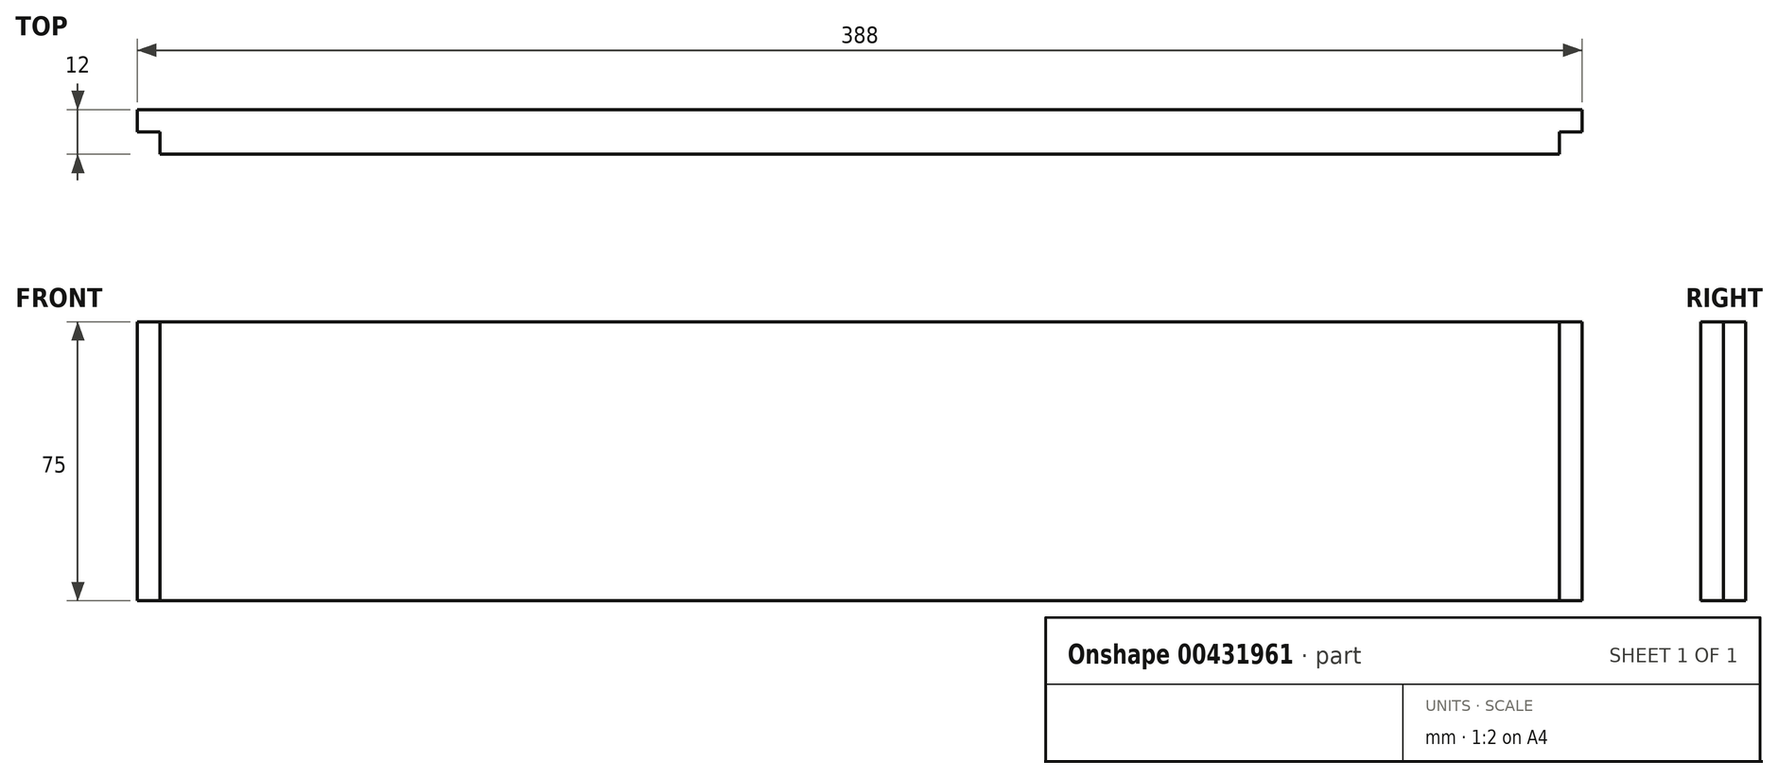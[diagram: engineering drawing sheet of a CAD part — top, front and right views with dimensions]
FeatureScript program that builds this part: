
annotation { "Feature Type Name" : "Feature", "Feature Type Description" : "" }
export const myFeature = defineFeature(function(context is Context, id is Id, definition is map)
    precondition{}
    {
        {
            var Q0;
            Q0=qCreatedBy(makeId("Front.planeOp"),FACE);
            var sketch = newSketch(context, id + "F0", { "sketchPlane" : qUnion([Q0])});
            skLineSegment(sketch, "E0.bottom", {"start": v(-183, 37.5) * mm, "end": v(205, 37.5) * mm});
            skLineSegment(sketch, "E0.top", {"start": v(-183, -37.5) * mm, "end": v(205, -37.5) * mm});
            skLineSegment(sketch, "E0.left", {"start": v(-183, 37.5) * mm, "end": v(-183, -37.5) * mm});
            skLineSegment(sketch, "E0.right", {"start": v(205, 37.5) * mm, "end": v(205, -37.5) * mm});
            skPoint(sketch, "E0.middle", {"position": v(11, 0) * mm});
            skSolve(sketch);
        }
        {
            var Q0;
            Q0=qSketchRegion(id+"F0",true);
            extrude(context, id + "F1", {"entities" : qUnion([Q0]), "depth" : 12 * mm, "offsetDistance" : 25 * mm});
        }
        {
            var Q0;
            Q0=makeQuery(id+"F1.opExtrude","CAP_FACE",FACE,{"disambiguationData":[OSD([sQuery(id+"F0.wireOp",EDGE,"E0.bottom"),sQuery(id+"F0.wireOp",EDGE,"E0.top"),sQuery(id+"F0.wireOp",EDGE,"E0.left"),sQuery(id+"F0.wireOp",EDGE,"E0.right")])],"isStart":false});
            var sketch = newSketch(context, id + "F2", { "sketchPlane" : qUnion([Q0])});
            skLineSegment(sketch, "E1.bottom", {"start": v(-183, 37.5) * mm, "end": v(-177, 37.5) * mm});
            skLineSegment(sketch, "E1.top", {"start": v(-183, -37.5) * mm, "end": v(-177, -37.5) * mm});
            skLineSegment(sketch, "E1.left", {"start": v(-183, 37.5) * mm, "end": v(-183, -37.5) * mm});
            skLineSegment(sketch, "E1.right", {"start": v(-177, 37.5) * mm, "end": v(-177, -37.5) * mm});
            skSolve(sketch);
        }
        {
            var Q0;
            Q0=qSketchRegion(id+"F2",true);
            extrude(context, id + "F3", {"entities" : qUnion([Q0]), "operationType" : NewBodyOperationType.REMOVE, "oppositeDirection" : true, "depth" : 6 * mm, "offsetDistance" : 25 * mm});
        }
        {
            var Q0;
            Q0=makeQuery(id+"F1.opExtrude","CAP_FACE",FACE,{"disambiguationData":[OSD([sQuery(id+"F0.wireOp",EDGE,"E0.bottom"),sQuery(id+"F0.wireOp",EDGE,"E0.top"),sQuery(id+"F0.wireOp",EDGE,"E0.left"),sQuery(id+"F0.wireOp",EDGE,"E0.right")])],"isStart":false});
            var sketch = newSketch(context, id + "F4", { "sketchPlane" : qUnion([Q0])});
            skLineSegment(sketch, "E2.bottom", {"start": v(205, 37.5) * mm, "end": v(199, 37.5) * mm});
            skLineSegment(sketch, "E2.top", {"start": v(205, -37.5) * mm, "end": v(199, -37.5) * mm});
            skLineSegment(sketch, "E2.left", {"start": v(205, 37.5) * mm, "end": v(205, -37.5) * mm});
            skLineSegment(sketch, "E2.right", {"start": v(199, 37.5) * mm, "end": v(199, -37.5) * mm});
            skSolve(sketch);
        }
        {
            var Q0;
            Q0=qSketchRegion(id+"F4",true);
            extrude(context, id + "F5", {"entities" : qUnion([Q0]), "operationType" : NewBodyOperationType.REMOVE, "oppositeDirection" : true, "depth" : 6 * mm, "offsetDistance" : 25 * mm});
        }
    });
